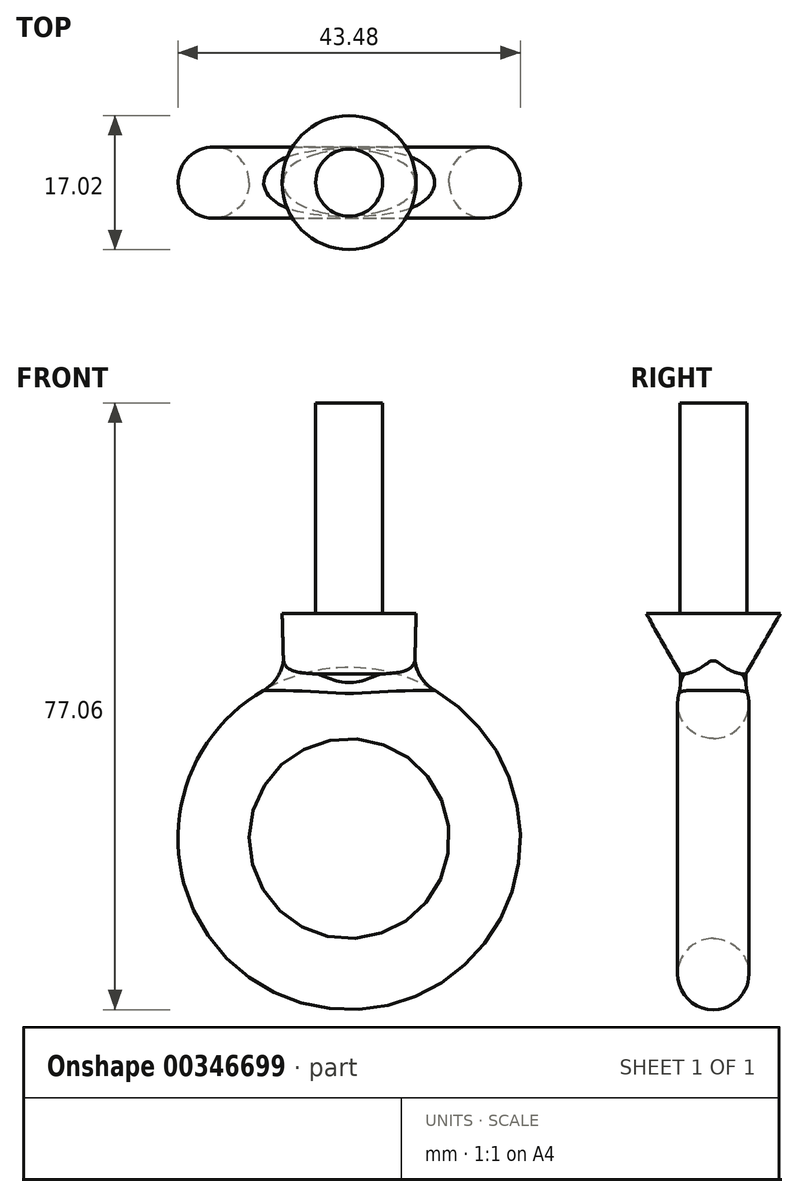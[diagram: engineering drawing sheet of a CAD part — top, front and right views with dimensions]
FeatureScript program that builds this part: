
annotation { "Feature Type Name" : "Feature", "Feature Type Description" : "" }
export const myFeature = defineFeature(function(context is Context, id is Id, definition is map)
    precondition{}
    {
        {
            var Q0;
            Q0=qCreatedBy(makeId("Top.planeOp"),FACE);
            var sketch = newSketch(context, id + "F0", { "sketchPlane" : qUnion([Q0])});
            skLineSegment(sketch, "E0", {"start": v(0, 0) * mm, "end": v(12.7, 0) * mm});
            skLineSegment(sketch, "E1", {"start": v(0, 0) * mm, "end": v(17.22, 0) * mm});
            skLineSegment(sketch, "E2", {"start": v(0, 0) * mm, "end": v(21.74, 0) * mm});
            skCircle(sketch, "E3", {"center": v(17.22, 0) * mm, "radius": 4.52 * mm});
            skLineSegment(sketch, "E4", {"start": v(0, 0) * mm, "end": v(0, 6.8) * mm});
            skSolve(sketch);
        }
        {
            var Q0;
            Q0 = qSketchRegion(id + "F0", true);
            var Q1;
            Q1=sQuery(id+"F0.wireOp",EDGE,"E4");
            revolve(context, id + "F1", {"entities" : qUnion([Q0]), "axis" : qUnion([Q1]), "revolveType" : RevolveType.FULL});
        }
        {
            var Q0;
            Q0=qCreatedBy(makeId("Top.planeOp"),FACE);
            cPlane(context, id + "F2", {"entities" : qUnion([Q0]), "cplaneType" : CPlaneType.OFFSET, "offset" : 28.57 * mm, "width" : 152.4 * mm, "height" : 152.4 * mm});
        }
        {
            var Q0;
            Q0=qCreatedBy(id+"F2.planeOp",FACE);
            var sketch = newSketch(context, id + "F3", { "sketchPlane" : qUnion([Q0])});
            skCircle(sketch, "E5", {"center": v(0, 0) * mm, "radius": 8.5 * mm});
            skSolve(sketch);
        }
        {
            var Q0;
            Q0=qCreatedBy(id+"F2.planeOp",FACE);
            cPlane(context, id + "F4", {"entities" : qUnion([Q0]), "cplaneType" : CPlaneType.OFFSET, "offset" : 7.65 * mm, "oppositeDirection" : true, "width" : 152.4 * mm, "height" : 152.4 * mm});
        }
        {
            var Q0;
            Q0=qCreatedBy(id+"F4.planeOp",FACE);
            var sketch = newSketch(context, id + "F5", { "sketchPlane" : qUnion([Q0])});
            skEllipse(sketch, "E6", {"center": v(0, 0) * mm, "majorRadius": 8.3 * mm, "minorRadius": 4.17 * mm, "majorAxis": v(1, 0)});
            skSolve(sketch);
        }
        {
            var Q1;
            Q1 = qSketchRegion(id + "F3", true);
            var Q2;
            Q2 = qSketchRegion(id + "F5", true);
            loft(context, id + "F6", {"operationType" : NewBodyOperationType.ADD, "sheetProfilesArray" : [{ "sheetProfileEntities" : qUnion([Q1]) }, { "sheetProfileEntities" : qUnion([Q2]) }]});
        }
        {
            var Q0;
            Q0=makeQuery(id+"F6.opLoft","CAP_FACE",FACE,{"disambiguationData":[OSD([makeQuery(id+"F5.imprint","IMPRINT",FACE,{"disambiguationData":[TD([[makeQuery(id+"F5.imprint","IMPRINT",EDGE,{"derivedFrom":sQuery(id+"F5.wireOp",EDGE,"E6")}),1.0]])]})])],"isStart":true});
            extrude(context, id + "F7", {"entities" : qUnion([Q0]), "operationType" : NewBodyOperationType.ADD, "depth" : 5.18 * mm});
        }
        {
            var Q0;
            Q0=makeQuery(id+"F6.opLoft","CAP_FACE",FACE,{"disambiguationData":[OSD([makeQuery(id+"F3.imprint","IMPRINT",FACE,{"disambiguationData":[TD([[makeQuery(id+"F3.imprint","IMPRINT",EDGE,{"derivedFrom":sQuery(id+"F3.wireOp",EDGE,"E5")}),1.0]])]})])],"isStart":true});
            var sketch = newSketch(context, id + "F8", { "sketchPlane" : qUnion([Q0])});
            skCircle(sketch, "E7", {"center": v(0, 0) * mm, "radius": 4.25 * mm});
            skSolve(sketch);
        }
        {
            var Q0;
            Q0 = qSketchRegion(id + "F8", true);
            extrude(context, id + "F9", {"entities" : qUnion([Q0]), "operationType" : NewBodyOperationType.ADD, "depth" : 26.75 * mm});
        }
        {
            var Q0;
            Q0=makeQuery(id+"F7.boolean.opBoolean","INTERSECT",EDGE,{"derivedFrom":[makeQuery(id+"F1.opRevolve","SWEPT_FACE",FACE,{"disambiguationData":[OSD([sQuery(id+"F0.wireOp",EDGE,"E3")])]}),makeQuery(id+"F7.opExtrude","SWEPT_FACE",FACE,{"disambiguationData":[OSD([sQuery(id+"F3.wireOp",EDGE,"E5"),sQuery(id+"F5.wireOp",EDGE,"E6")])]})]});
            fillet(context, id + "F10", {"entities" : qUnion([Q0]), "radius" : 5.08 * mm, "tangentPropagation" : true, "allowEdgeOverflow" : false});
        }
    });
